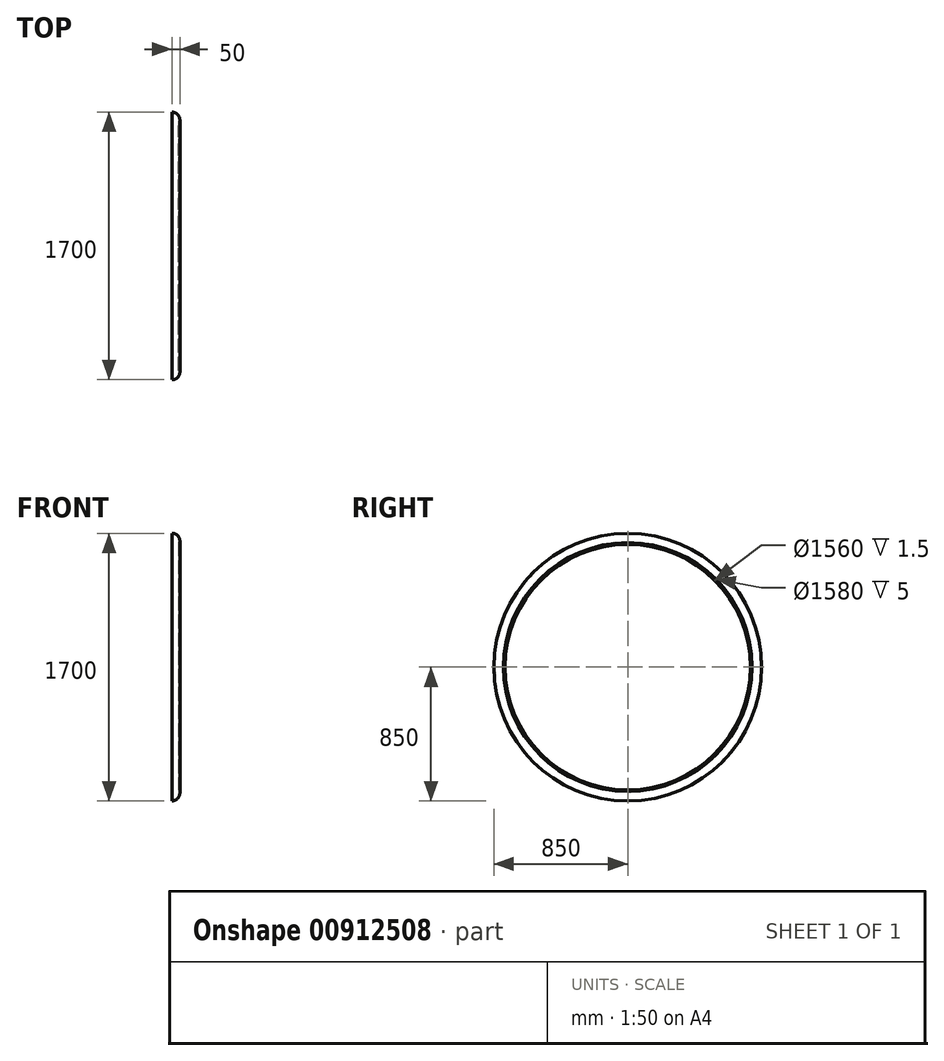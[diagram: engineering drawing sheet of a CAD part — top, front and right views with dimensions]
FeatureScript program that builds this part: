
annotation { "Feature Type Name" : "Feature", "Feature Type Description" : "" }
export const myFeature = defineFeature(function(context is Context, id is Id, definition is map)
    precondition{}
    {
        {
            var Q0;
            Q0=qCreatedBy(makeId("Front.planeOp"),FACE);
            var sketch = newSketch(context, id + "F0", { "sketchPlane" : qUnion([Q0])});
            skArc(sketch, "E0", {"start": v(-50, 0) * mm, "mid": v(-35.36, 35.36) * mm, "end": v(0, 50) * mm});
            skLineSegment(sketch, "E1", {"start": v(-50, 0) * mm, "end": v(-50, -10) * mm});
            skLineSegment(sketch, "E2", {"start": v(-50, -10) * mm, "end": v(-45, -10) * mm});
            skLineSegment(sketch, "E3", {"start": v(-45, -10) * mm, "end": v(-45, -20) * mm});
            skLineSegment(sketch, "E4", {"start": v(-45, -20) * mm, "end": v(-42, -20) * mm});
            skLineSegment(sketch, "E5", {"start": v(-42, -20) * mm, "end": v(-42, -7) * mm});
            skLineSegment(sketch, "E6", {"start": v(-42, -7) * mm, "end": v(-47, -7) * mm});
            skLineSegment(sketch, "E7", {"start": v(-47, -7) * mm, "end": v(-47, 0) * mm});
            skArc(sketch, "E8", {"start": v(-47, 0) * mm, "mid": v(-33.23, 33.23) * mm, "end": v(0, 47) * mm});
            skLineSegment(sketch, "E9", {"start": v(0, 50) * mm, "end": v(0, 47) * mm});
            skArc(sketch, "E10.MirrorCS", {"start": v(47, 0) * mm, "mid": v(33.23, 33.23) * mm, "end": v(0, 47) * mm});
            skArc(sketch, "E11.MirrorCS", {"start": v(50, 0) * mm, "mid": v(35.36, 35.36) * mm, "end": v(0, 50) * mm});
            skLineSegment(sketch, "E12.MirrorCS", {"start": v(45, -10) * mm, "end": v(45, -20) * mm});
            skLineSegment(sketch, "E13.MirrorCS", {"start": v(50, -10) * mm, "end": v(45, -10) * mm});
            skLineSegment(sketch, "E14.MirrorCS", {"start": v(42, -7) * mm, "end": v(47, -7) * mm});
            skLineSegment(sketch, "E15.MirrorCS", {"start": v(42, -20) * mm, "end": v(42, -7) * mm});
            skLineSegment(sketch, "E16.MirrorCS", {"start": v(45, -20) * mm, "end": v(42, -20) * mm});
            skLineSegment(sketch, "E17.MirrorCS", {"start": v(50, 0) * mm, "end": v(50, -10) * mm});
            skLineSegment(sketch, "E18.MirrorCS", {"start": v(47, -7) * mm, "end": v(47, 0) * mm});
            skSolve(sketch);
        }
        {
            var Q0;
            Q0=qCreatedBy(makeId("Right.planeOp"),FACE);
            var sketch = newSketch(context, id + "F1", { "sketchPlane" : qUnion([Q0])});
            skLineSegment(sketch, "E19", {"start": v(0, 50) * mm, "end": v(0, -800) * mm});
            skSolve(sketch);
        }
        {
            var Q0;
            Q0=qCreatedBy(makeId("Front.planeOp"),FACE);
            var sketch = newSketch(context, id + "F2", { "sketchPlane" : qUnion([Q0])});
            skLineSegment(sketch, "E20", {"start": v(-100.18, -800) * mm, "end": v(122.99, -800) * mm});
            skSolve(sketch);
        }
        {
            var Q0;
            Q0=makeQuery(id+"F0.imprint","IMPRINT",FACE,{"disambiguationData":[TD([[makeQuery(id+"F0.imprint","IMPRINT",EDGE,{"derivedFrom":sQuery(id+"F0.wireOp",EDGE,"E0")}),-1.0]])]});
            var Q1;
            Q1=makeQuery(id+"F0.imprint","IMPRINT",FACE,{"disambiguationData":[TD([[makeQuery(id+"F0.imprint","IMPRINT",EDGE,{"derivedFrom":sQuery(id+"F0.wireOp",EDGE,"E9")}),1.0]])]});
            var Q2;
            Q2=sQuery(id+"F2.wireOp",EDGE,"E20");
            revolve(context, id + "F3", {"surfaceOperationType" : NewSurfaceOperationType.NEW, "entities" : qUnion([Q0, Q1]), "axis" : qUnion([Q2]), "revolveType" : RevolveType.FULL});
        }
        {
            var Q0;
            Q0=makeQuery(id+"F3.opRevolve","SWEPT_EDGE",EDGE,{"disambiguationData":[OSD([sQuery(id+"F0.wireOp",EDGE,"E12.MirrorCS"),sQuery(id+"F0.wireOp",EDGE,"E16.MirrorCS")])]});
            fillet(context, id + "F4", {"entities" : qUnion([Q0]), "radius" : 1.5 * mm, "tangentPropagation" : true, "allowEdgeOverflow" : false});
        }
    });
